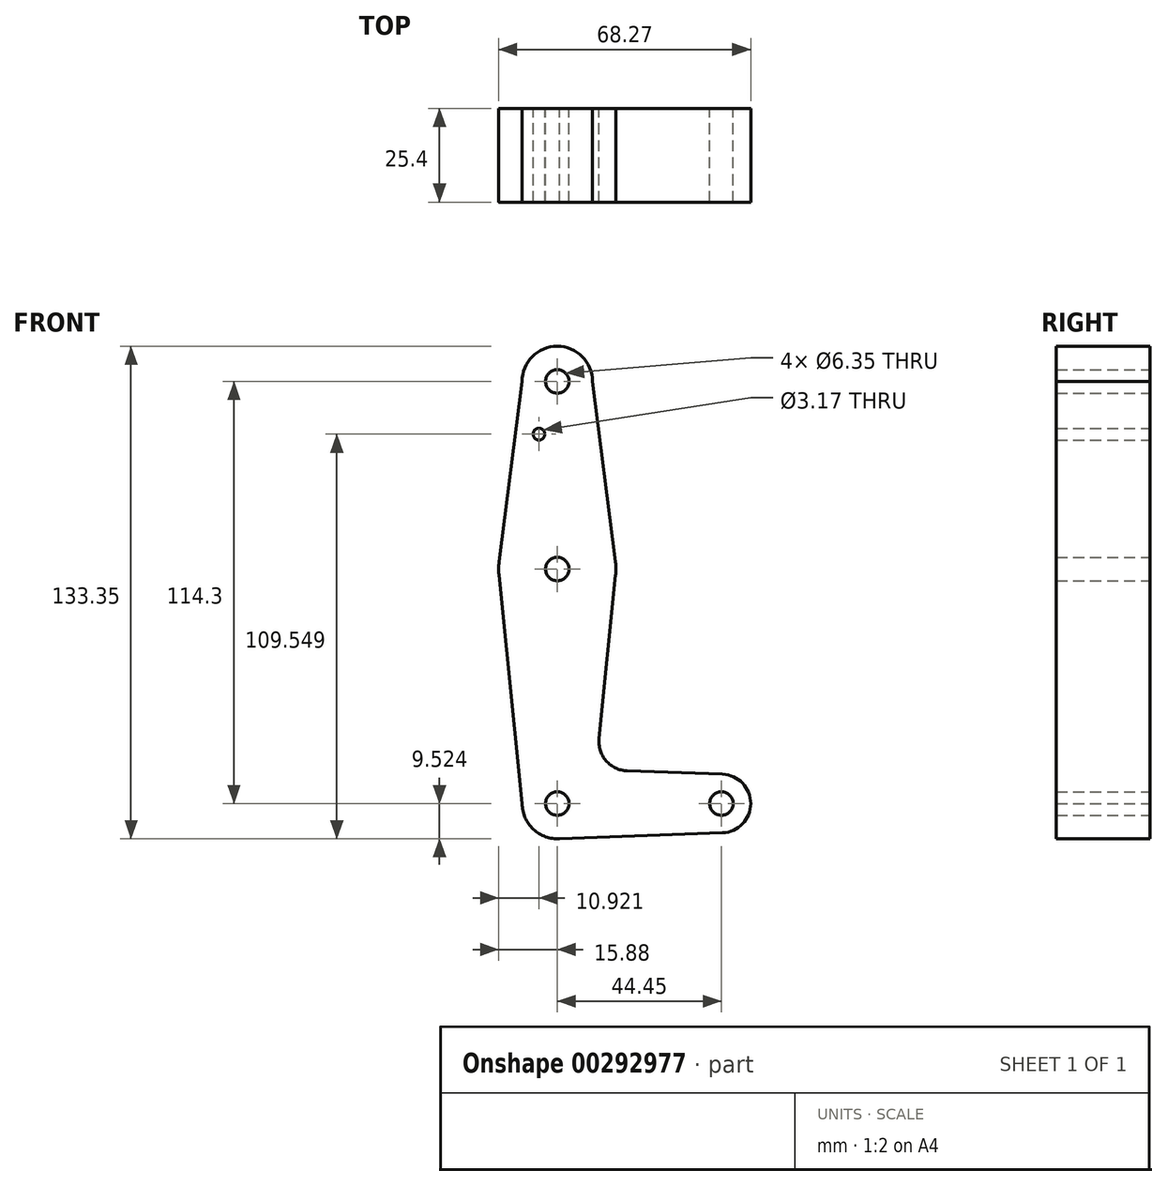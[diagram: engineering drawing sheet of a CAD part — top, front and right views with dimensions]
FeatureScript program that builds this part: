
annotation { "Feature Type Name" : "Feature", "Feature Type Description" : "" }
export const myFeature = defineFeature(function(context is Context, id is Id, definition is map)
    precondition{}
    {
        {
            var Q0;
            Q0=qCreatedBy(makeId("Front.planeOp"),FACE);
            var sketch = newSketch(context, id + "F0", { "sketchPlane" : qUnion([Q0])});
            skCircle(sketch, "E0", {"center": v(0, 70.52) * mm, "radius": 9.53 * mm});
            skCircle(sketch, "E1", {"center": v(0, -43.78) * mm, "radius": 9.53 * mm});
            skCircle(sketch, "E2", {"center": v(0, 19.72) * mm, "radius": 15.88 * mm});
            skCircle(sketch, "E3", {"center": v(44.45, -43.78) * mm, "radius": 7.94 * mm});
            skLineSegment(sketch, "E4", {"start": v(0, 70.52) * mm, "end": v(0, 19.72) * mm, "construction": true});
            skLineSegment(sketch, "E5", {"start": v(0, 19.72) * mm, "end": v(0, -43.78) * mm, "construction": true});
            skLineSegment(sketch, "E6", {"start": v(0, -43.78) * mm, "end": v(44.45, -43.78) * mm, "construction": true});
            skLineSegment(sketch, "E7", {"start": v(-9.53, 70.52) * mm, "end": v(-15.75, 21.73) * mm});
            skLineSegment(sketch, "E8", {"start": v(-9.53, -43.78) * mm, "end": v(-15.8, 18.12) * mm});
            skLineSegment(sketch, "E9", {"start": v(11.3, -26.18) * mm, "end": v(15.8, 18.12) * mm});
            skLineSegment(sketch, "E10", {"start": v(9.53, 70.52) * mm, "end": v(15.75, 21.73) * mm});
            skLineSegment(sketch, "E11", {"start": v(18.93, -34.93) * mm, "end": v(44.73, -35.84) * mm});
            skLineSegment(sketch, "E12", {"start": v(0, -53.3) * mm, "end": v(44.73, -51.7) * mm});
            skCircle(sketch, "E13", {"center": v(0, 70.52) * mm, "radius": 3.18 * mm});
            skCircle(sketch, "E14", {"center": v(0, 19.72) * mm, "radius": 3.18 * mm});
            skCircle(sketch, "E15", {"center": v(0, -43.78) * mm, "radius": 3.18 * mm});
            skCircle(sketch, "E16", {"center": v(44.45, -43.78) * mm, "radius": 3.18 * mm});
            skCircle(sketch, "E17", {"center": v(-4.96, 56.25) * mm, "radius": 1.59 * mm});
            skPoint(sketch, "E18.newPointA", {"position": v(0, -34.25) * mm});
            skArc(sketch, "E18.filletArc", {"start": v(11.3, -26.18) * mm, "mid": v(13.22, -32.2) * mm, "end": v(18.93, -34.93) * mm});
            skSolve(sketch);
        }
        {
            var Q0;
            Q0 = qSketchRegion(id + "F0", true);
            extrude(context, id + "F1", {"entities" : qUnion([Q0]), "depth" : 25.4 * mm});
        }
    });
